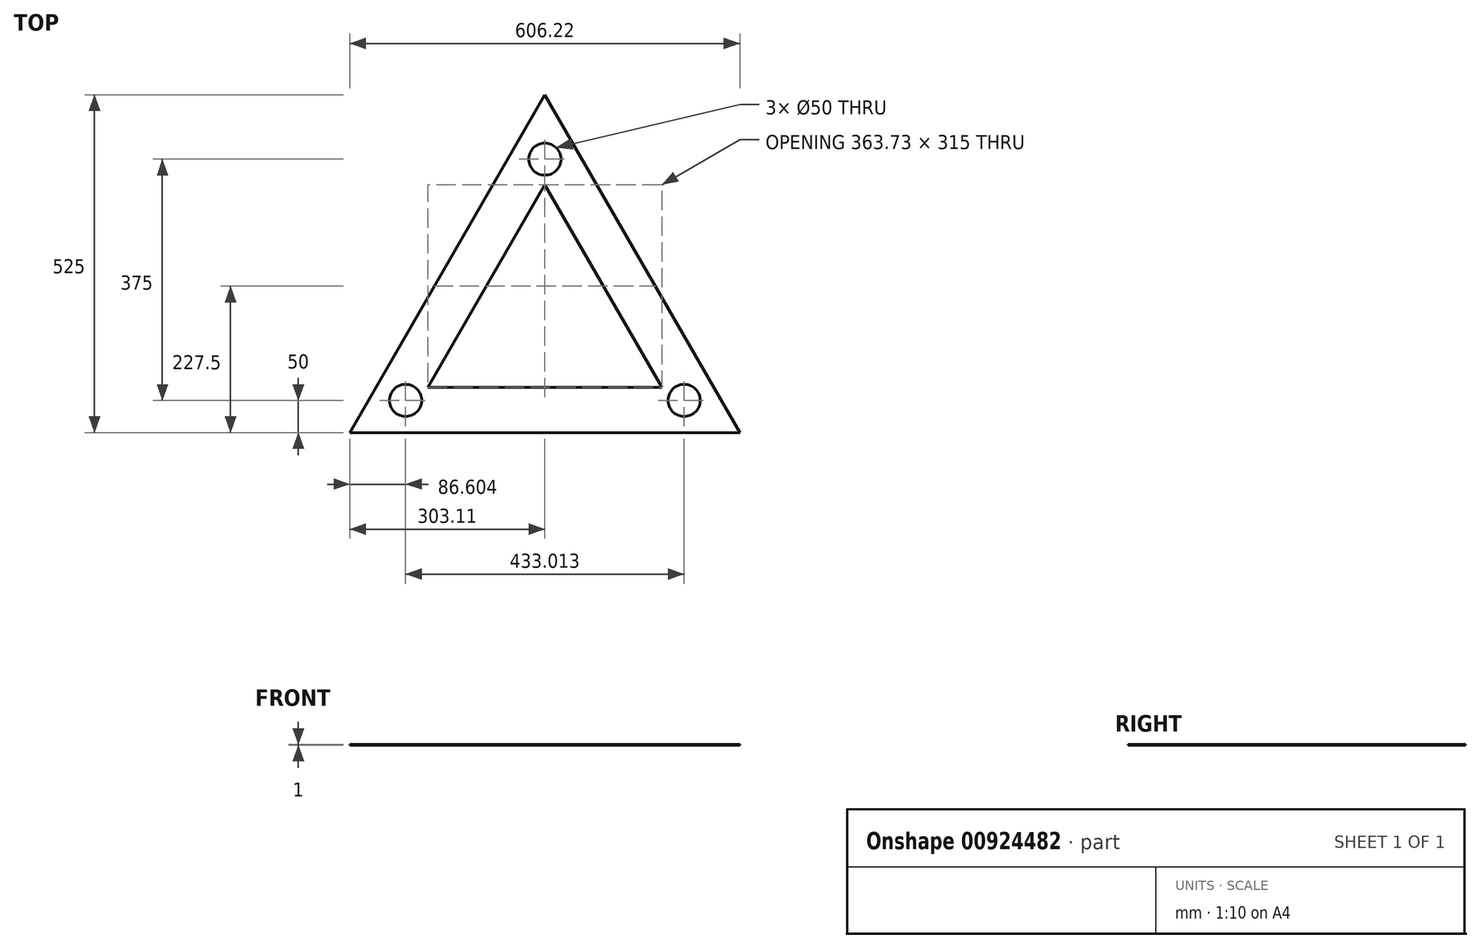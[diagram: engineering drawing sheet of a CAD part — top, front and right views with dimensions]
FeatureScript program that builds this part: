
annotation { "Feature Type Name" : "Feature", "Feature Type Description" : "" }
export const myFeature = defineFeature(function(context is Context, id is Id, definition is map)
    precondition{}
    {
        {
            var Q0;
            Q0=qCreatedBy(makeId("Top.planeOp"),FACE);
            var sketch = newSketch(context, id + "F0", { "sketchPlane" : qUnion([Q0])});
            skLineSegment(sketch, "E0", {"start": v(-433.01, -250) * mm, "end": v(0, 500) * mm});
            skLineSegment(sketch, "E1", {"start": v(0, 500) * mm, "end": v(433.01, -250) * mm});
            skLineSegment(sketch, "E2", {"start": v(433.01, -250) * mm, "end": v(-433.01, -250) * mm});
            skCircle(sketch, "E3", {"center": v(0, 0) * mm, "radius": 400 * mm});
            skLineSegment(sketch, "E4", {"start": v(-346.41, -200) * mm, "end": v(0, 400) * mm});
            skLineSegment(sketch, "E5", {"start": v(0, 400) * mm, "end": v(346.41, -200) * mm});
            skLineSegment(sketch, "E6", {"start": v(346.41, -200) * mm, "end": v(-346.41, -200) * mm});
            skCircle(sketch, "E7", {"center": v(0, 400) * mm, "radius": 25 * mm});
            skCircle(sketch, "E8", {"center": v(-346.41, -200) * mm, "radius": 25 * mm});
            skCircle(sketch, "E9", {"center": v(346.41, -200) * mm, "radius": 25 * mm});
            skCircle(sketch, "E10.cCircle", {"center": v(0, 0) * mm, "radius": 334.43 * mm, "construction": true});
            skLineSegment(sketch, "E10.0", {"start": v(0, 334.43) * mm, "end": v(289.63, -167.22) * mm});
            skLineSegment(sketch, "E10.1", {"start": v(289.63, -167.22) * mm, "end": v(-289.63, -167.22) * mm});
            skLineSegment(sketch, "E10.2", {"start": v(-289.63, -167.22) * mm, "end": v(0, 334.43) * mm});
            skLineSegment(sketch, "E11", {"start": v(0, 400) * mm, "end": v(-216.5, 25) * mm});
            skLineSegment(sketch, "E12", {"start": v(-216.5, 25) * mm, "end": v(216.5, 25) * mm});
            skLineSegment(sketch, "E13", {"start": v(216.5, 25) * mm, "end": v(0, 400) * mm});
            skLineSegment(sketch, "E14", {"start": v(0, 500) * mm, "end": v(-303.1, -25) * mm});
            skLineSegment(sketch, "E15", {"start": v(-303.1, -25) * mm, "end": v(303.1, -25) * mm});
            skLineSegment(sketch, "E16", {"start": v(0, 334.43) * mm, "end": v(-178.65, 25) * mm});
            skLineSegment(sketch, "E17", {"start": v(-178.65, 25) * mm, "end": v(178.65, 25) * mm});
            skLineSegment(sketch, "E18", {"start": v(178.65, 25) * mm, "end": v(0, 334.43) * mm});
            skCircle(sketch, "E19", {"center": v(-216.5, 25) * mm, "radius": 25 * mm});
            skCircle(sketch, "E20", {"center": v(216.5, 25) * mm, "radius": 25 * mm});
            skSolve(sketch);
        }
        {
            var Q0;
            Q0=qCreatedBy(makeId("Top.planeOp"),FACE);
            var sketch = newSketch(context, id + "F1", { "sketchPlane" : qUnion([Q0])});
            skCircle(sketch, "E21.cCircle", {"center": v(0, 0) * mm, "radius": 250 * mm, "construction": true});
            skLineSegment(sketch, "E21.0", {"start": v(0, 250) * mm, "end": v(216.5, -125) * mm});
            skLineSegment(sketch, "E21.1", {"start": v(216.5, -125) * mm, "end": v(-216.5, -125) * mm});
            skLineSegment(sketch, "E21.2", {"start": v(-216.5, -125) * mm, "end": v(0, 250) * mm});
            skCircle(sketch, "E22", {"center": v(-216.5, -125) * mm, "radius": 25 * mm});
            skCircle(sketch, "E23", {"center": v(0, 250) * mm, "radius": 25 * mm});
            skCircle(sketch, "E24", {"center": v(216.5, -125) * mm, "radius": 25 * mm});
            skCircle(sketch, "E25.cCircle", {"center": v(0, 0) * mm, "radius": 350 * mm, "construction": true});
            skLineSegment(sketch, "E25.0", {"start": v(0, 350) * mm, "end": v(303.1, -175) * mm});
            skLineSegment(sketch, "E25.1", {"start": v(303.1, -175) * mm, "end": v(-303.1, -175) * mm});
            skLineSegment(sketch, "E25.2", {"start": v(-303.1, -175) * mm, "end": v(0, 350) * mm});
            skCircle(sketch, "E26.cCircle", {"center": v(0, 0) * mm, "radius": 210 * mm, "construction": true});
            skLineSegment(sketch, "E26.0", {"start": v(0, 210) * mm, "end": v(181.87, -105) * mm});
            skLineSegment(sketch, "E26.1", {"start": v(181.87, -105) * mm, "end": v(-181.87, -105) * mm});
            skLineSegment(sketch, "E26.2", {"start": v(-181.87, -105) * mm, "end": v(0, 210) * mm});
            skSolve(sketch);
        }
        {
            var Q0;
            Q0=makeQuery(id+"F1.imprint","IMPRINT",FACE,{"disambiguationData":[TD([[makeQuery(id+"F1.imprint","IMPRINT",EDGE,{"derivedFrom":sQuery(id+"F1.wireOp",EDGE,"E25.0")}),-1.0]])]});
            var Q1;
            Q1=makeQuery(id+"F1.imprint","IMPRINT",FACE,{"disambiguationData":[TD([[makeQuery(id+"F1.imprint","IMPRINT",EDGE,{"derivedFrom":sQuery(id+"F1.wireOp",EDGE,"E26.0")}),1.0]])]});
            extrude(context, id + "F2", {"entities" : qUnion([Q0, Q1]), "depth" : 1 * mm, "offsetDistance" : 25 * mm});
        }
    });
